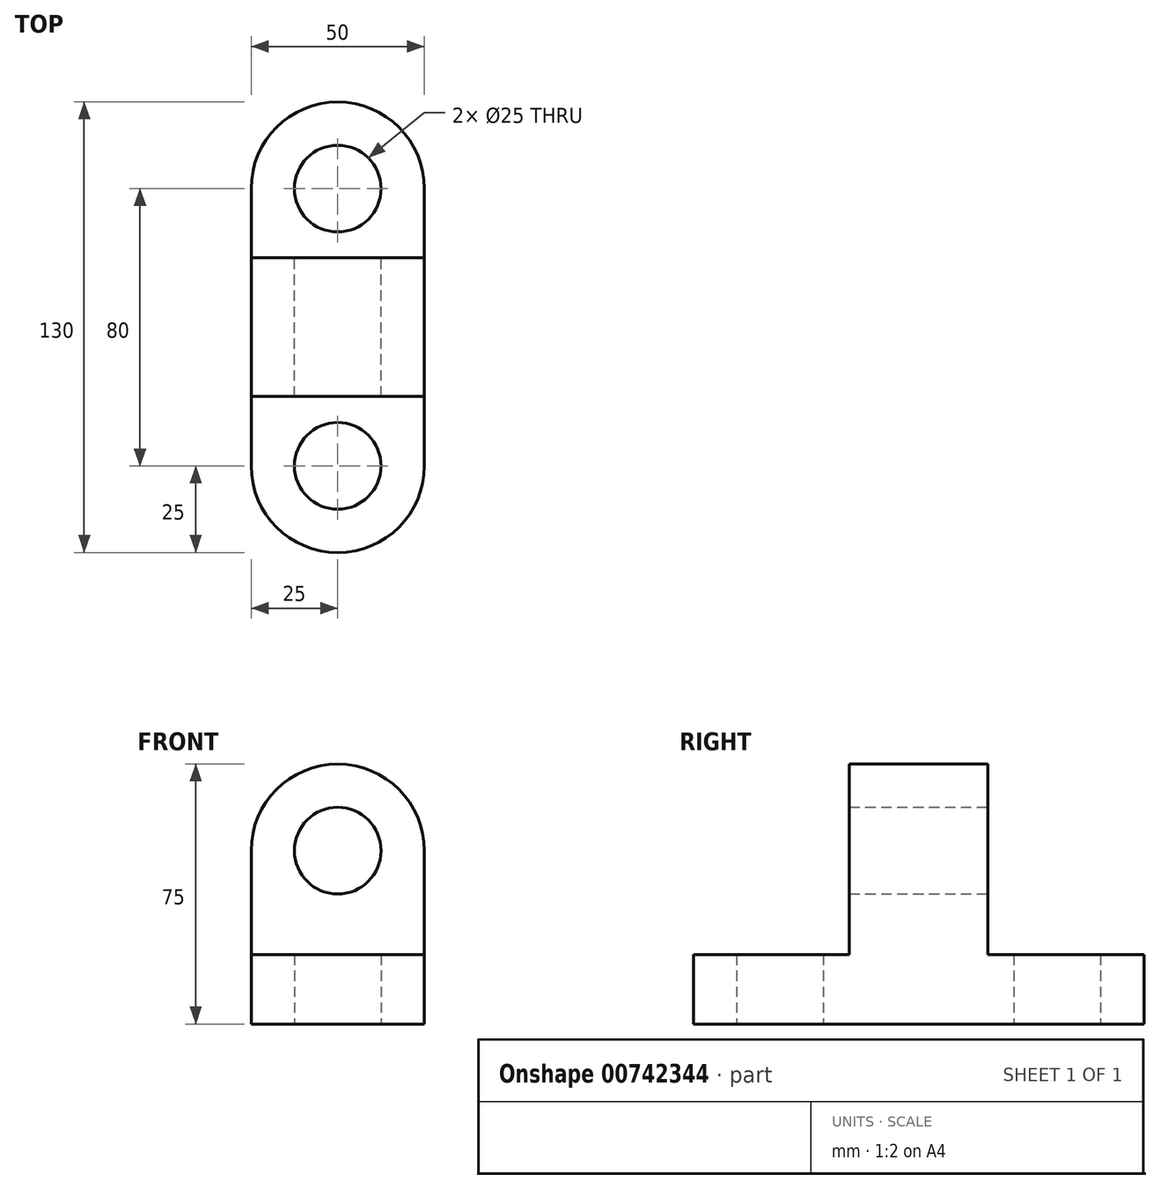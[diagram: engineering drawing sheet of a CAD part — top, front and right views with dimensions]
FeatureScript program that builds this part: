
annotation { "Feature Type Name" : "Feature", "Feature Type Description" : "" }
export const myFeature = defineFeature(function(context is Context, id is Id, definition is map)
    precondition{}
    {
        {
            var Q0;
            Q0=qCreatedBy(makeId("Front.planeOp"),FACE);
            var sketch = newSketch(context, id + "F0", { "sketchPlane" : qUnion([Q0])});
            skLineSegment(sketch, "E0.top", {"start": v(25, 50) * mm, "end": v(-25, 50) * mm});
            skArc(sketch, "E1", {"start": v(25, 50) * mm, "mid": v(0, 75) * mm, "end": v(-25, 50) * mm});
            skCircle(sketch, "E2", {"center": v(0, 50) * mm, "radius": 12.5 * mm});
            skLineSegment(sketch, "E3", {"start": v(-25, 50) * mm, "end": v(-25, 0) * mm});
            skLineSegment(sketch, "E4", {"start": v(25, 50) * mm, "end": v(25, 0) * mm});
            skLineSegment(sketch, "E5", {"start": v(0, 74.93) * mm, "end": v(0, -65.01) * mm, "construction": true});
            skLineSegment(sketch, "E6", {"start": v(-25, 0) * mm, "end": v(25, 0) * mm});
            skSolve(sketch);
        }
        {
            var Q0;
            Q0 = qSketchRegion(id + "F0", true);
            extrude(context, id + "F1", {"entities" : qUnion([Q0]), "depth" : 40 * mm, "offsetDistance" : 25 * mm});
        }
        {
            var Q0;
            Q0=qCreatedBy(makeId("Top.planeOp"),FACE);
            var sketch = newSketch(context, id + "F2", { "sketchPlane" : qUnion([Q0])});
            skLineSegment(sketch, "E7", {"start": v(-25, 0) * mm, "end": v(-25, 20) * mm});
            skLineSegment(sketch, "E8", {"start": v(25, 0) * mm, "end": v(25, 20) * mm});
            skLineSegment(sketch, "E9", {"start": v(-25, 20) * mm, "end": v(25, 20) * mm});
            skArc(sketch, "E10", {"start": v(25, 20) * mm, "mid": v(0, 45) * mm, "end": v(-25, 20) * mm});
            skCircle(sketch, "E11", {"center": v(0, 20) * mm, "radius": 12.5 * mm});
            skLineSegment(sketch, "E12", {"start": v(-25, 0) * mm, "end": v(25, 0) * mm});
            skLineSegment(sketch, "E13", {"start": v(25, 0) * mm, "end": v(25, -40) * mm});
            skLineSegment(sketch, "E14", {"start": v(25, -40) * mm, "end": v(-25, -40) * mm});
            skLineSegment(sketch, "E15", {"start": v(-25, -40) * mm, "end": v(-25, 0) * mm});
            skLineSegment(sketch, "E16", {"start": v(25, -40) * mm, "end": v(25, -60) * mm});
            skLineSegment(sketch, "E17", {"start": v(25, -60) * mm, "end": v(-25, -60) * mm});
            skLineSegment(sketch, "E18", {"start": v(-25, -60) * mm, "end": v(-25, -40) * mm});
            skArc(sketch, "E19", {"start": v(-25, -60) * mm, "mid": v(0, -85) * mm, "end": v(25, -60) * mm});
            skCircle(sketch, "E20", {"center": v(0, -60) * mm, "radius": 12.5 * mm});
            skLineSegment(sketch, "E21", {"start": v(0, 20) * mm, "end": v(0, -60) * mm, "construction": true});
            skSolve(sketch);
        }
        {
            var Q0;
            Q0 = qSketchRegion(id + "F2", true);
            extrude(context, id + "F3", {"entities" : qUnion([Q0]), "operationType" : NewBodyOperationType.ADD, "depth" : 20 * mm, "offsetDistance" : 25 * mm});
        }
    });
